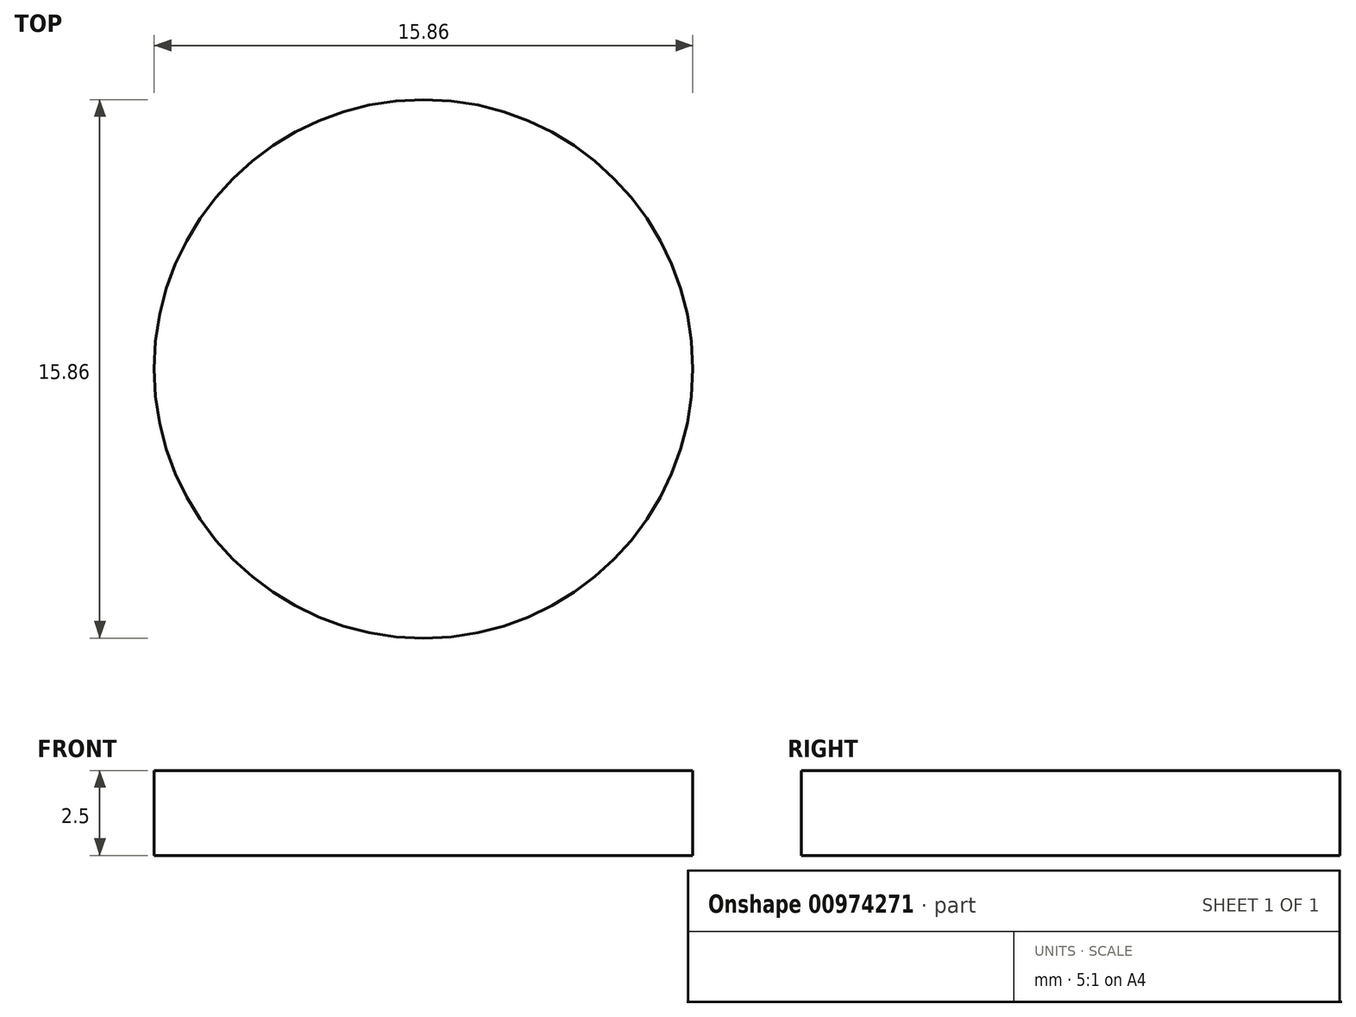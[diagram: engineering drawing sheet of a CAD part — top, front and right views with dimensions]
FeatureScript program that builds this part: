
annotation { "Feature Type Name" : "Feature", "Feature Type Description" : "" }
export const myFeature = defineFeature(function(context is Context, id is Id, definition is map)
    precondition{}
    {
        {
            var Q0;
            Q0=qCreatedBy(makeId("Top.planeOp"),FACE);
            var sketch = newSketch(context, id + "F0", { "sketchPlane" : qUnion([Q0])});
            skCircle(sketch, "E0", {"center": v(0, 0) * mm, "radius": 7.93 * mm});
            skSolve(sketch);
        }
        {
            var Q0;
            Q0 = qSketchRegion(id + "F0", true);
            extrude(context, id + "F1", {"entities" : qUnion([Q0]), "depth" : 2 * mm, "offsetDistance" : 25 * mm});
        }
        {
            var Q0;
            Q0 = qSketchRegion(id + "F0", true);
            extrude(context, id + "F2", {"entities" : qUnion([Q0]), "operationType" : NewBodyOperationType.ADD, "oppositeDirection" : true, "depth" : 0.5 * mm, "offsetDistance" : 25 * mm});
        }
    });
